# Revit family: Artisan Mediterranean
name_source: partatom
category: Generic Models
revit_build: Autodesk Revit 2017 (Build: 20160225_1515(x64)
units: mm (PartAtom-declared; Revit-internal decimal feet)

## family parameters
Always vertical = Yes
Can host rebar = No
Cut with Voids When Loaded = No
Part Type = Normal
Room Calculation Point = No
Round Connector Dimension = Use Diameter
Shared = No
Work Plane-Based = Yes

## types (1)
- Artisan Mediterranean
    Bottom Rail = 0' - 3 1/4"
    Default Elevation = 4' - 0"
    Finish Color = Default
    Hinge Point = 2' - 5 1/4"
    Lower Louver Section Angle = 20.00°
    Lower Louver Section Height = 2' - 2"
    Lower Louver Section Top Rail = 0' - 1 1/2"
    Lower Louver Section Width = 1' - 2"
    Manufacturer = New Horizon Shutters
    Mid Rail Height = 2' - 6"
    Model = Artisan Mediterranean
    Mounting Width = 1' - 2"
    Shutter Height = 5' - 4"
    Shutter Width = 1' - 6"
    Top Rail = 0' - 3 1/4"
    URL = www.newhorizonshutters.com

## geometry (parser evidence)
native form markers: Sweep x21
no freeform markers — native parametric forms only
